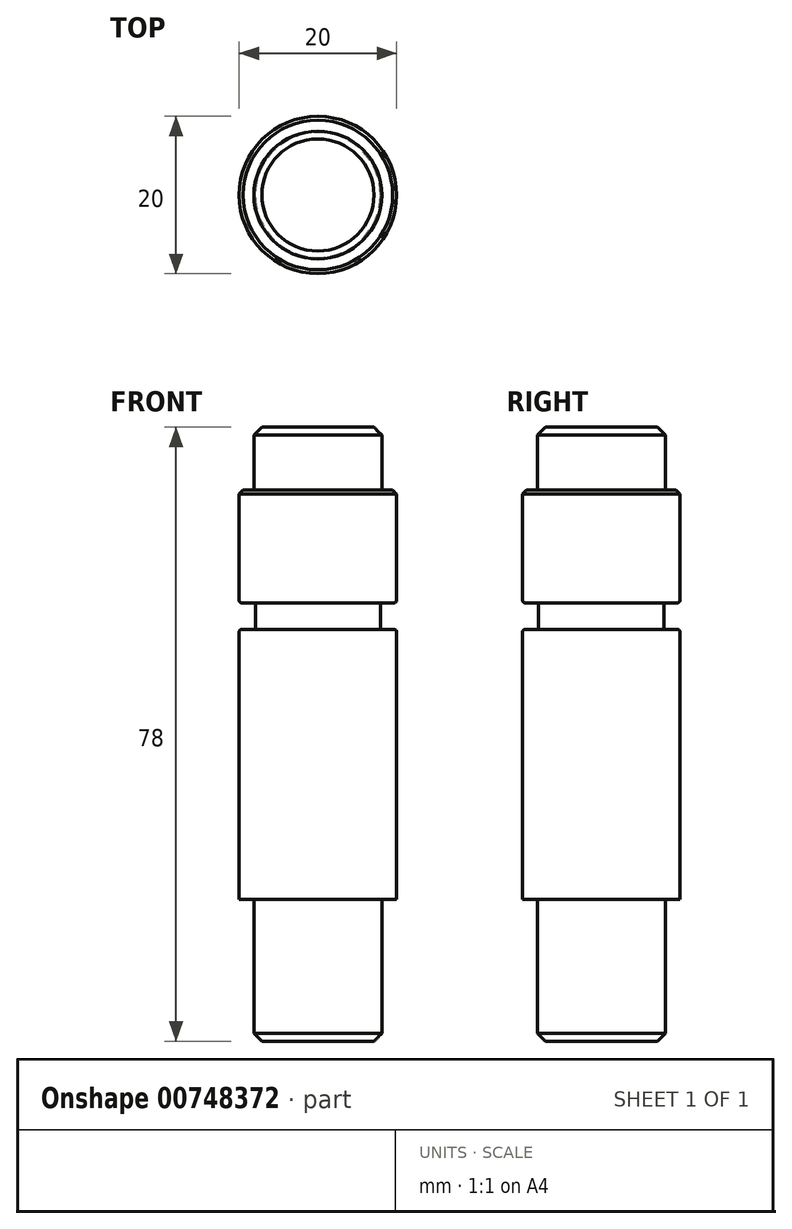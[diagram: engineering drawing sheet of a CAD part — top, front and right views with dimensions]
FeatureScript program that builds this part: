
annotation { "Feature Type Name" : "Feature", "Feature Type Description" : "" }
export const myFeature = defineFeature(function(context is Context, id is Id, definition is map)
    precondition{}
    {
        {
            var Q0;
            Q0=qCreatedBy(makeId("Top.planeOp"),FACE);
            var sketch = newSketch(context, id + "F0", { "sketchPlane" : qUnion([Q0])});
            skCircle(sketch, "E0", {"center": v(0, 0) * mm, "radius": 8.12 * mm});
            skSolve(sketch);
        }
        {
            var Q0;
            Q0 = qSketchRegion(id + "F0", true);
            extrude(context, id + "F1", {"entities" : qUnion([Q0]), "depth" : 18 * mm, "offsetDistance" : 25 * mm});
        }
        {
            var Q0;
            Q0=makeQuery(id+"F1.opExtrude","CAP_EDGE",EDGE,{"disambiguationData":[OSD([sQuery(id+"F0.wireOp",EDGE,"E0")])],"isStart":true});
            chamfer(context, id + "F2", {"entities" : qUnion([Q0]), "width" : 1 * mm, "tangentPropagation" : true});
        }
        {
            var Q0;
            Q0=makeQuery(id+"F1.opExtrude","CAP_FACE",FACE,{"disambiguationData":[OSD([sQuery(id+"F0.wireOp",EDGE,"E0")])],"isStart":false});
            var sketch = newSketch(context, id + "F3", { "sketchPlane" : qUnion([Q0])});
            skCircle(sketch, "E1", {"center": v(0, 0) * mm, "radius": 10 * mm});
            skSolve(sketch);
        }
        {
            var Q0;
            Q0 = qSketchRegion(id + "F3", true);
            extrude(context, id + "F4", {"entities" : qUnion([Q0]), "operationType" : NewBodyOperationType.ADD, "depth" : 34.3 * mm, "offsetDistance" : 25 * mm});
        }
        {
            var Q0;
            Q0=makeQuery(id+"F4.opExtrude","CAP_FACE",FACE,{"disambiguationData":[OSD([sQuery(id+"F3.wireOp",EDGE,"E1")])],"isStart":false});
            var sketch = newSketch(context, id + "F5", { "sketchPlane" : qUnion([Q0])});
            skCircle(sketch, "E2", {"center": v(0, 0) * mm, "radius": 7.95 * mm});
            skSolve(sketch);
        }
        {
            var Q0;
            Q0 = qSketchRegion(id + "F5", true);
            extrude(context, id + "F6", {"entities" : qUnion([Q0]), "operationType" : NewBodyOperationType.ADD, "depth" : 3.4 * mm, "offsetDistance" : 25 * mm});
        }
        {
            var Q0;
            Q0=makeQuery(id+"F6.opExtrude","CAP_FACE",FACE,{"disambiguationData":[OSD([sQuery(id+"F5.wireOp",EDGE,"E2")])],"isStart":false});
            var sketch = newSketch(context, id + "F7", { "sketchPlane" : qUnion([Q0])});
            skSolve(sketch);
        }
        {
            var Q0;
            Q0=makeQuery(id+"F7.imprint","IMPRINT",FACE,{"disambiguationData":[TD([[makeQuery(id+"F7.imprint","IMPRINT",EDGE,{"derivedFrom":makeQuery(id+"F6.opExtrude","CAP_EDGE",EDGE,{"disambiguationData":[OSD([sQuery(id+"F5.wireOp",EDGE,"E2")])],"isStart":false})}),1.0]])]});
            var sketch = newSketch(context, id + "F8", { "sketchPlane" : qUnion([Q0])});
            skCircle(sketch, "E3", {"center": v(0, 0) * mm, "radius": 10 * mm});
            skSolve(sketch);
        }
        {
            var Q0;
            Q0 = qSketchRegion(id + "F8", true);
            extrude(context, id + "F9", {"entities" : qUnion([Q0]), "operationType" : NewBodyOperationType.ADD, "depth" : 14.3 * mm, "offsetDistance" : 25 * mm});
        }
        {
            var Q0;
            Q0=makeQuery(id+"F9.opExtrude","CAP_FACE",FACE,{"disambiguationData":[OSD([sQuery(id+"F8.wireOp",EDGE,"E3")])],"isStart":false});
            var sketch = newSketch(context, id + "F10", { "sketchPlane" : qUnion([Q0])});
            skCircle(sketch, "E4", {"center": v(0, 0) * mm, "radius": 8.12 * mm});
            skSolve(sketch);
        }
        {
            var Q0;
            Q0 = qSketchRegion(id + "F10", true);
            extrude(context, id + "F11", {"entities" : qUnion([Q0]), "operationType" : NewBodyOperationType.ADD, "depth" : 8 * mm, "offsetDistance" : 25 * mm});
        }
        {
            var Q0;
            Q0=makeQuery(id+"F11.opExtrude","CAP_EDGE",EDGE,{"disambiguationData":[OSD([sQuery(id+"F10.wireOp",EDGE,"E4")])],"isStart":false});
            chamfer(context, id + "F12", {"entities" : qUnion([Q0]), "width" : 1 * mm, "tangentPropagation" : true});
        }
        {
            var Q0;
            Q0=makeQuery(id+"F9.opExtrude","CAP_EDGE",EDGE,{"disambiguationData":[OSD([sQuery(id+"F8.wireOp",EDGE,"E3")])],"isStart":false});
            chamfer(context, id + "F13", {"entities" : qUnion([Q0]), "width" : 0.5 * mm, "tangentPropagation" : true});
        }
        {
            var Q0;
            Q0=makeQuery(id+"F9.opExtrude","CAP_EDGE",EDGE,{"disambiguationData":[OSD([sQuery(id+"F8.wireOp",EDGE,"E3")])],"isStart":true});
            var Q1;
            Q1=makeQuery(id+"F4.opExtrude","CAP_EDGE",EDGE,{"disambiguationData":[OSD([sQuery(id+"F3.wireOp",EDGE,"E1")])],"isStart":false});
            fillet(context, id + "F14", {"entities" : qUnion([Q0, Q1]), "radius" : 0.3 * mm, "tangentPropagation" : true, "allowEdgeOverflow" : false});
        }
    });
